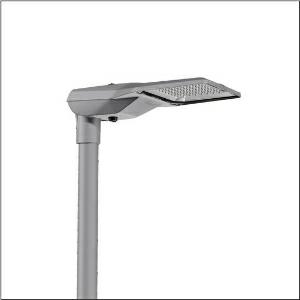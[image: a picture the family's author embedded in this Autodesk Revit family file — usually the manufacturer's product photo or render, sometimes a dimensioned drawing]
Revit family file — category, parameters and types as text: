
# Revit family: streetlight_sl_21_midi___stw1_0a_5xe3e33t08lb_0cd5
name_source: partatom
category: Lighting Fixtures
units: mm (PartAtom-declared; Revit-internal decimal feet)

## family parameters
Cut with Voids When Loaded = No
Host = Face
Light Source = No
Part Type = Normal
Room Calculation Point = No
Round Connector Dimension = Use Diameter
Shared = No

## types (1)
- --- (1 x LED, 14340 lm, 99.6 W, 3000K)
    Apparent Load = 100 VA
    CIE Flux Codes = 38 75 98 100 100
    Color Rendering = 70
    Color Temperature = 3000K
    Default Elevation = 1800 mm
    Description = Streetlight SL 21 midi, mast luminaire, primary light control with lens, of PMMA, primary optical cover: cover, of toughened safety glass, transparent, light distribution: STW1.0a, light emission: direct distribution, primary light characteristic: asymmetric, installation type: side-entry, post-top, LED, High Power LED, rated luminous flux: 14.340lm, luminous efficacy: 144lm/W, light colour: 730, colour temperature: 3000K, control gear: D4i, control: overheat protection, constant luminous flux control, time-dependent luminous flux control, flexible luminous flux parameterisation, pre-setting: logarithmic dimming characteristic, mains connection: 230..240V, AC, 50/60Hz, start of lifetime: 100W, end of service life: 102W, reduction: 46W, luminaire housing, of diecast aluminium, powder-coated, Siteco® metallic grey (DB 702S), corrosivity category C5 mid according to DIN EN ISO 12944, please order mast flange separately, inclination adjustable: 0°, 5°, 10°, 15°, sealing non-destructively replaceable, multi-level sealing system, length: 644mm, width: 335mm, height: 110mm, mast flange for spigot size: 42mm (side-entry): 5XC10008XM4, 60/48mm (side-entry/post-top): 5XC10108XM2, 76/60mm (side-entry/post-top): 5XC10108XM1, mounting height: 4..8m, Smart Interface below and above, protection rating (complete): IP66, insulation class (complete): insulation class II (safety insulation), certification: CE, ENEC, ENEC+, VDE, impact resistance: IK10, permissible operating ambient temperature for outdoor applications: -40..+50°C, standard-compliant lighting for roads and squares, packaging unit: 1 piece

Light Distribution: STW1.0a
    Height = 111 mm
    Lamp = 1 x LED
    Lamp Light Flux = 14340 lm
    Lamp Power = 99.6 W
    Lamp count = 1
    Length = 644 mm
    Luminous efficacy = 144 lm/W
    Manufacturer = Siteco
    ModVariant = No
    Model = 5XE3E33T08LB
    Number of Poles = 1
    OnlyDefault = Yes
    Power Factor = 1
    Product Name = Streetlight SL 21 midi | STW1.0a
    Product group = mast luminaire | pylon top
    ProductGroupID = 6100
    Protection Class = Protection class II
    Protection Degree = IP 66
    RLX_Detail_Level = 1
    RLX_Emergency_Light_Flux = 0 lm
    RLX_Emergency_Type = 0
    RLX_Emergency_Type_DB = No
    RlxData = <blob elided: 26997 chars, md5=3d051259>
    Socket = socket
    Standby Power = 0 W
    System Light Flux = 14340 lm
    System Power = 100 W
    Type Comments = factory setting: luminous flux: 100 % | dim-lin: 254 | 1020 mA
    Type Image = l_1004304.jpg
    URL = http://relux.com
    VarID = @adj_031667
    Voltage = 0 V
    Weight = 0.00 kg
    Width = 336 mm

## geometry (parser evidence)
native form markers: Blend x4, Sweep x10
no freeform markers — native parametric forms only
